# Revit family: 57_CRD_ME_S_Fan
name_source: partatom
category: Mechanical Equipment
units: mm (PartAtom-declared; Revit-internal decimal feet)

## family parameters
Always vertical = Yes
Cut with Voids When Loaded = No
OmniClass Number = 23.75.70.21.24
OmniClass Title = Air Terminal Units
Part Type = Normal
Room Calculation Point = Yes
Round Connector Dimension = Use Diameter
Shared = No
Work Plane-Based = Yes

## types (2) — shared parameters
Article Description = Ventilation unit
Base Family Version = 12.19
Content Supplier URL = www.MEPcontent.com
Custom = No
Default Elevation = 1219.2 mm  [stored 4 ft]
Depth = 114 mm  [stored 0.374016 ft]
Description = Ventilation unit
EMCS Version = 4.0
ETIM Article Class = EC010004
Family Version = 11.17
Grille  Rectangular = Rectangular Grille
Grille  Square = Square Grille
Height = 350 mm  [stored 1.14829 ft]
IFCExportAs = IfcAirTerminal
MEPcontent Class = VENTILATION_UNIT
Manufacturer = ClimaRad
Manufacturer URL = https://www.climarad.nl
Mechanical Flow max = 250.0 m³/h
Mechanical Flow nom = 50.0 m³/h
Product Line = ClimaRad
Revit Version = 2018
URL = https://mep.trimble.com
Voltage = 230 V
Width = 350 mm  [stored 1.14829 ft]
zero-valued in all types: Cost

## per-type parameters (varying)
| type | Electrical Heating | Manufacturer Art. No. |
| S-Fan Plus | 800 W | 4510600 |
| S-Fan | 0 W | 4510500 |

note: column(s) folded — value = type name in every type: Article Type, Model

note: [stored X ft] marks values corroborated as IEEE doubles in the binary element streams (Revit-internal decimal feet)

## geometry (parser evidence)
native form markers: Sweep x9
no freeform markers — native parametric forms only
